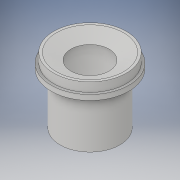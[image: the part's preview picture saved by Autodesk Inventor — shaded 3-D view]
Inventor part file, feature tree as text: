
AUTODESK INVENTOR PART (.ipt)
format: ipt  version: 2017 (Build 210142000, 142)  size: 158,720 bytes
history: native  units: in
note: dims shown in document units (in); Inventor stores cm internally (conversion verified against a paired STEP export)
features: revolve x1, sketch x1
ambient origin geometry x8: Origin, YZ Plane, XZ Plane, XY Plane, X Axis, Y Axis, Z Axis, Center Point
bodies: Body1 (feature_tree)
feature tree (2):
  revolve  "Revolution2"  [1 undecoded]
  sketch  "Sketch1"  dims[d0=1.13in d1=3.75in d2=0.25in d3=0.1718in d5=1.0in d6=1.0in d7=90.0deg d8=0.5in d9=15.0deg d11=0.25in d12=1.25in d13=0.25in d15=0.25in d16=0.5in d17=0.5in d18=0.5in d19=2.5in d20=0.5in d22=0.375in d23=0.25in d25=0.234in d26=15.0deg d28=90.0deg]
note: 1 required parameter value undecoded (feature->parameter linkage not recoverable at this tier; creation-order binding heuristic only, values carry confidence <= 0.55)
